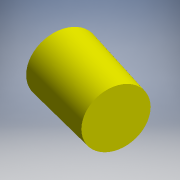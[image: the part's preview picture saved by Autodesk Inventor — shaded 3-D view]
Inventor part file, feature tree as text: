
AUTODESK INVENTOR PART (.ipt)
format: ipt  version: 2017.3 (Build 213256000, 256)  size: 96,768 bytes
history: native  units: mm (DEFAULTED — no unit token found)
features: other x7, revolve x1, sketch x1
ambient origin geometry x8: Origin, YZ Plane, XZ Plane, XY Plane, X Axis, Y Axis, Z Axis, Center Point
bodies: Solid1 (feature_tree)
feature tree (9):
  revolve  "Revolution1"  [1 undecoded]
  other  "roller_XY"
  other  "roller_YZ"
  other  "roller_ZX"
  other  "roller_X"
  other  "roller_Y"
  other  "roller_Z"
  other  "roller_Center"
  sketch  "Sketch_2"  dims[d0=360.0deg]
note: 1 required parameter value undecoded (feature->parameter linkage not recoverable at this tier; creation-order binding heuristic only, values carry confidence <= 0.55)
